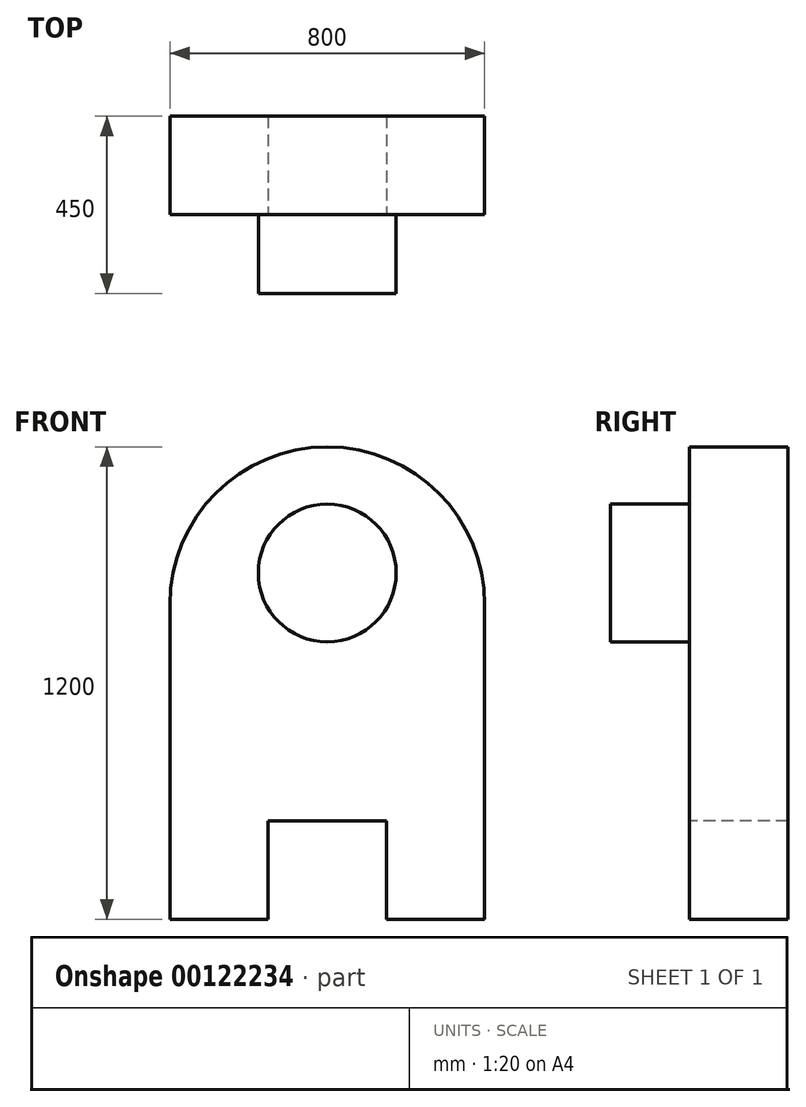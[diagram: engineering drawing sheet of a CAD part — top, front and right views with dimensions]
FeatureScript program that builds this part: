
annotation { "Feature Type Name" : "Feature", "Feature Type Description" : "" }
export const myFeature = defineFeature(function(context is Context, id is Id, definition is map)
    precondition{}
    {
        {
            var Q0;
            Q0=qCreatedBy(makeId("Front.planeOp"),FACE);
            var sketch = newSketch(context, id + "F0", { "sketchPlane" : qUnion([Q0])});
            skLineSegment(sketch, "E0.bottom", {"start": v(-400, -400) * mm, "end": v(400, -400) * mm});
            skLineSegment(sketch, "E0.left", {"start": v(-400, -400) * mm, "end": v(-400, 400) * mm});
            skLineSegment(sketch, "E0.right", {"start": v(400, -400) * mm, "end": v(400, 400) * mm});
            skPoint(sketch, "E0.middle", {"position": v(0, 0) * mm});
            skArc(sketch, "E1", {"start": v(400, 400) * mm, "mid": v(0, 800) * mm, "end": v(-400, 400) * mm});
            skSolve(sketch);
        }
        {
            var Q0;
            Q0 = qSketchRegion(id + "F0", true);
            extrude(context, id + "F1", {"entities" : qUnion([Q0]), "depth" : 250 * mm});
        }
        {
            var Q0;
            Q0=makeQuery(id+"F1.opExtrude","CAP_FACE",FACE,{"disambiguationData":[OSD([sQuery(id+"F0.wireOp",EDGE,"E0.bottom"),sQuery(id+"F0.wireOp",EDGE,"E0.left"),sQuery(id+"F0.wireOp",EDGE,"E0.right"),sQuery(id+"F0.wireOp",EDGE,"E1")])],"isStart":false});
            var sketch = newSketch(context, id + "F2", { "sketchPlane" : qUnion([Q0])});
            skLineSegment(sketch, "E2.top", {"start": v(150, -150) * mm, "end": v(-150, -150) * mm});
            skLineSegment(sketch, "E2.left", {"start": v(150, -400) * mm, "end": v(150, -150) * mm});
            skLineSegment(sketch, "E3", {"start": v(-150, -400) * mm, "end": v(150, -400) * mm});
            skLineSegment(sketch, "E4", {"start": v(-150, -150) * mm, "end": v(-150, -400) * mm});
            skSolve(sketch);
        }
        {
            var Q0;
            Q0 = qSketchRegion(id + "F2", true);
            extrude(context, id + "F3", {"entities" : qUnion([Q0]), "operationType" : NewBodyOperationType.REMOVE, "endBound" : BoundingType.THROUGH_ALL, "oppositeDirection" : true, "depth" : 25 * mm});
        }
        {
            var Q0;
            Q0=makeQuery(id+"F1.opExtrude","CAP_FACE",FACE,{"disambiguationData":[OSD([sQuery(id+"F0.wireOp",EDGE,"E0.bottom"),sQuery(id+"F0.wireOp",EDGE,"E0.left"),sQuery(id+"F0.wireOp",EDGE,"E0.right"),sQuery(id+"F0.wireOp",EDGE,"E1")])],"isStart":false});
            var sketch = newSketch(context, id + "F4", { "sketchPlane" : qUnion([Q0])});
            skCircle(sketch, "E5", {"center": v(0, 479.76) * mm, "radius": 175 * mm});
            skSolve(sketch);
        }
        {
            var Q0;
            Q0 = qSketchRegion(id + "F4", true);
            extrude(context, id + "F5", {"entities" : qUnion([Q0]), "operationType" : NewBodyOperationType.ADD, "depth" : 200 * mm});
        }
    });
